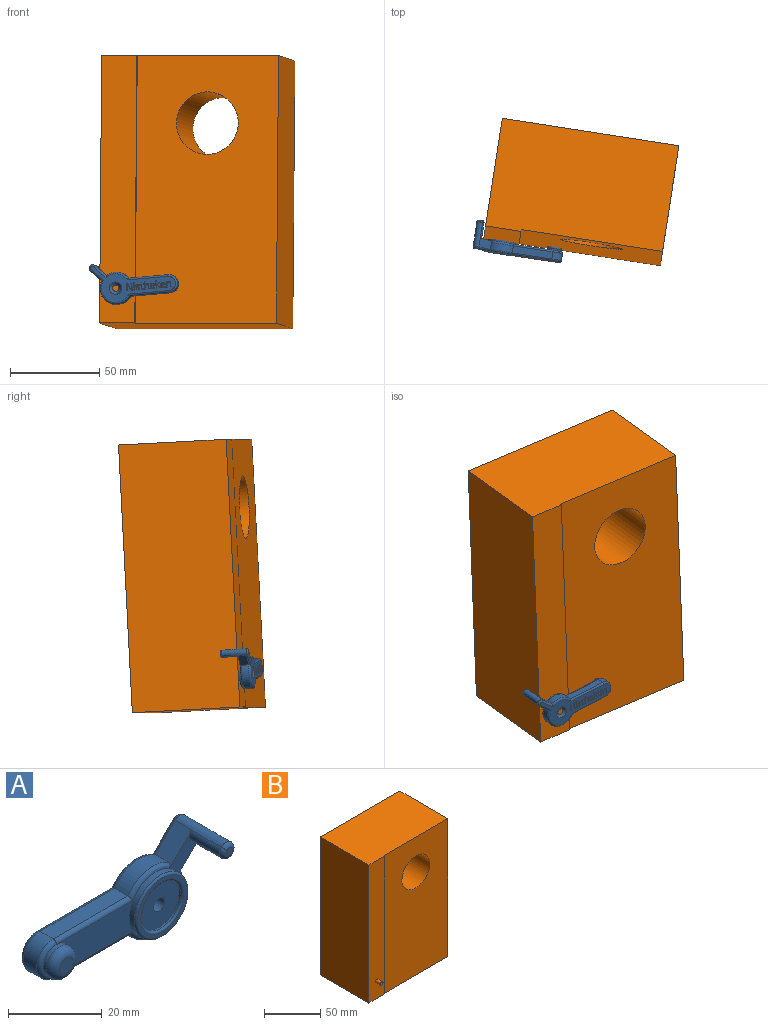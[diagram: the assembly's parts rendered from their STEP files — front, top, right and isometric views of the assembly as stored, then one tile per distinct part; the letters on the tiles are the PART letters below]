
ASSEMBLY  parts=2 mates=1
PART A: 218 faces, bbox 49.6x16x23.9 mm
  f0: plane 47.2x21.2mm, normal (0,1,0), area 355.5mm2, adj f16,f23,f24,f25,f26,f27,f28,f29
  f1: plane 23.07x8mm, normal (0,-1,0), area 153.6mm2, adj f12,f13,f32,f35
  f2: plane 9.55x9.55mm, normal (0,-1,0), area 31.1mm2, adj f7,f9,f13,f21
  f3: cylinder r=1.7mm len=5.23mm, axis (0,1,0), area 55.9mm2, adj f16,f18
  f4: cylinder r=5mm len=10mm, axis (0,1,0), area 62.8mm2, adj f5,f11,f24,f33
  f5: plane 22.52x4mm, normal (0,0,-1), area 90.1mm2, adj f4,f6,f26,f32
  f6: cylinder r=9mm len=16.48mm, axis (0,1,0), area 112.1mm2, adj f5,f7,f28,f31
  f7: plane 6.72x6.72mm, normal (0.71,0,-0.71), area 42.6mm2, adj f2,f6,f8,f30,f31
  f8: extruded ~14x3.41mm, area 88mm2, adj f7,f9,f21,f29,f37
  f9: plane 6.72x6.72mm, normal (-0.71,0,0.71), area 42.6mm2, adj f2,f8,f10,f27,f34
  f10: cylinder r=9mm len=12.27mm, axis (0,1,0), area 55.6mm2, adj f9,f11,f25,f34
  f11: plane 22.52x4mm, normal (0,0,1), area 90.1mm2, adj f4,f10,f23,f35
  f12: cylinder r=4mm len=8mm, axis (0,1,0), area 25.1mm2, adj f1,f33,f38
  f13: cylinder r=8mm len=16mm, axis (0,1,0), area 75.4mm2, adj f1,f2,f20,f31,f34
  f14: plane 15x15mm, normal (0,-1,0), area 44mm2, adj f19,f20
  f15: plane 4x4mm, normal (0,-1,0), area 12.6mm2, adj f38
  f16: cone r=1.7mm half-angle=45deg, axis (0,1,0), area 40.7mm2, adj f0,f3
  f17: cylinder r=6mm len=12mm, axis (0,-1,0), area 18.8mm2, adj f18,f19
  f18: plane 12x12mm, normal (0,-1,0), area 104mm2, adj f3,f17
  f19: torus R=6.5mm, axis (0,-1,0), area 30.5mm2, adj f14,f17
  f20: torus R=7.5mm, axis (0,-1,0), area 38.6mm2, adj f13,f14
  f21: cylinder r=2mm len=9mm, axis (0,1,0), area 56.5mm2, adj f2,f8,f36
  f22: plane 2x2mm, normal (0,-1,0), area 3.1mm2, adj f36,f37
  f23: cylinder r=1mm len=23.07mm, axis (-1,0,0), area 35.7mm2, adj f0,f11,f24,f25
  f24: torus R=4mm, axis (0,-1,0), area 22.9mm2, adj f0,f4,f23,f26
  f25: torus R=8mm, axis (0,-1,0), area 21.7mm2, adj f0,f10,f23,f27
  f26: cylinder r=1mm len=23.07mm, axis (1,0,0), area 35.7mm2, adj f0,f5,f24,f28
  f27: cylinder r=1mm len=7.29mm, axis (-0.71,0,-0.71), area 13.8mm2, adj f0,f9,f25,f29
  f28: torus R=8mm, axis (0,-1,0), area 43mm2, adj f0,f6,f26,f30
  f29: bspline ~4.36x4.36mm, area 8.1mm2, adj f0,f8,f27,f30
  f30: cylinder r=1mm len=7.29mm, axis (0.71,0,0.71), area 13.8mm2, adj f0,f7,f28,f29
  f31: torus R=8mm, axis (0,-1,0), area 42.4mm2, adj f6,f7,f13,f32
  f32: cylinder r=1mm len=23.07mm, axis (-1,0,0), area 35.7mm2, adj f1,f5,f31,f33
  f33: torus R=4mm, axis (0,-1,0), area 22.9mm2, adj f4,f12,f32,f35
  f34: torus R=8mm, axis (0,-1,0), area 21.1mm2, adj f9,f10,f13,f35
  f35: cylinder r=1mm len=23.07mm, axis (1,0,0), area 35.7mm2, adj f1,f11,f33,f34
  f36: torus R=1mm, axis (0,-1,0), area 8.1mm2, adj f21,f22,f37
  f37: bspline ~4.36x3.77mm, area 8.1mm2, adj f8,f22,f36
  f38: torus R=2mm, axis (0,-1,0), area 64.6mm2, adj f12,f15
  f39: plane 2.97x1mm, normal (1,0,0), area 3mm2, adj f0,f40,f42,f43
  f40: plane 1x0.45mm, normal (0,0,1), area 0.5mm2, adj f0,f39,f41,f43
  f41: plane 2.97x1mm, normal (-1,0,0), area 3mm2, adj f0,f40,f42,f43
  f42: plane 1x0.45mm, normal (0,0,-1), area 0.5mm2, adj f0,f39,f41,f43
  f43: plane 2.97x0.45mm, normal (0,1,0), area 1.3mm2, adj f39,f40,f41,f42
  f44: extruded ~1x0.23mm, area 0.2mm2, adj f0,f45,f51,f52
  f45: extruded ~1x0.23mm, area 0.2mm2, adj f0,f44,f46,f52
  f46: extruded ~1x0.19mm, area 0.2mm2, adj f0,f45,f47,f52
  f47: extruded ~1x0.19mm, area 0.2mm2, adj f0,f46,f48,f52
  f48: extruded ~1x0.23mm, area 0.2mm2, adj f0,f47,f49,f52
  f49: extruded ~1x0.23mm, area 0.2mm2, adj f0,f48,f50,f52
  f50: extruded ~1x0.19mm, area 0.2mm2, adj f0,f49,f51,f52
  f51: extruded ~1x0.19mm, area 0.2mm2, adj f0,f44,f50,f52
  f52: plane 0.6x0.53mm, normal (0,1,0), area 0.3mm2, adj f44,f45,f46,f47,f48,f49,f50,f51
  f53: extruded ~1x0.49mm, area 0.5mm2, adj f0,f54,f77,f78
  f54: extruded ~1x0.64mm, area 0.7mm2, adj f0,f53,f55,f78
  f55: extruded ~1x0.87mm, area 0.9mm2, adj f0,f54,f56,f78
  f56: extruded ~1x0.92mm, area 1mm2, adj f0,f55,f57,f78
  f57: plane 1x0.42mm, normal (-1,0,0), area 0.4mm2, adj f0,f56,f58,f78
  f58: extruded ~1x0.46mm, area 0.5mm2, adj f0,f57,f59,f78
  f59: extruded ~1x0.47mm, area 0.5mm2, adj f0,f58,f60,f78
  f60: extruded ~1x0.54mm, area 0.6mm2, adj f0,f59,f61,f78
  f61: extruded ~1x0.34mm, area 0.4mm2, adj f0,f60,f62,f78
  f62: extruded ~1x0.3mm, area 0.3mm2, adj f0,f61,f63,f78
  f63: extruded ~1x0.59mm, area 0.7mm2, adj f0,f62,f64,f78
  f64: extruded ~1x0.59mm, area 0.6mm2, adj f0,f63,f65,f78
  f65: extruded ~1x0.26mm, area 0.4mm2, adj f0,f64,f66,f78
  f66: extruded ~1x0.35mm, area 0.4mm2, adj f0,f65,f67,f78
  f67: extruded ~1x0.57mm, area 0.7mm2, adj f0,f66,f68,f78
  f68: extruded ~1x0.81mm, area 0.9mm2, adj f0,f67,f69,f78
  f69: extruded ~1x0.94mm, area 1mm2, adj f0,f68,f70,f78
  f70: plane 1x0.37mm, normal (0.92,0,0.4), area 0.4mm2, adj f0,f69,f71,f78
  f71: extruded ~1x0.81mm, area 0.8mm2, adj f0,f70,f72,f78
  f72: extruded ~1x0.48mm, area 0.5mm2, adj f0,f71,f73,f78
  f73: extruded ~1x0.28mm, area 0.3mm2, adj f0,f72,f74,f78
  f74: extruded ~1x0.2mm, area 0.2mm2, adj f0,f73,f75,f78
  f75: extruded ~1x0.2mm, area 0.3mm2, adj f0,f74,f76,f78
  f76: extruded ~1x0.52mm, area 0.6mm2, adj f0,f75,f77,f78
  f77: extruded ~1x0.71mm, area 0.8mm2, adj f0,f53,f76,f78
  f78: plane 3.08x2.11mm, normal (0,1,0), area 2.7mm2, adj f53,f54,f55,f56,f57,f58,f59,f60
  f79: extruded ~1x0.35mm, area 0.4mm2, adj f0,f80,f97,f98
  f80: extruded ~1x0.23mm, area 0.2mm2, adj f0,f79,f81,f98
  f81: extruded ~1x0.18mm, area 0.2mm2, adj f0,f80,f82,f98
  f82: plane 1x0.34mm, normal (1,0,0), area 0.3mm2, adj f0,f81,f83,f98
  f83: extruded ~1x0.22mm, area 0.2mm2, adj f0,f82,f84,f98
  f84: extruded ~1x0.26mm, area 0.3mm2, adj f0,f83,f85,f98
  f85: extruded ~1x0.91mm, area 1.4mm2, adj f0,f84,f86,f98
  f86: plane 1.77x1mm, normal (-1,0,0), area 1.8mm2, adj f0,f85,f87,f98
  f87: plane 1x0.43mm, normal (0,0,1), area 0.4mm2, adj f0,f86,f88,f98
  f88: plane 1x0.22mm, normal (-1,0,0), area 0.2mm2, adj f0,f87,f89,f98
  f89: plane 1x0.43mm, normal (-0.4,0,-0.92), area 0.5mm2, adj f0,f88,f90,f98
  f90: plane 1x0.63mm, normal (-0.96,0,-0.29), area 0.7mm2, adj f0,f89,f91,f98
  f91: plane 1x0.26mm, normal (0,0,-1), area 0.3mm2, adj f0,f90,f92,f98
  f92: plane 1x0.69mm, normal (1,0,0), area 0.7mm2, adj f0,f91,f93,f98
  f93: plane 1x0.86mm, normal (0,0,-1), area 0.9mm2, adj f0,f92,f94,f98
  f94: plane 1x0.35mm, normal (1,0,0), area 0.3mm2, adj f0,f93,f95,f98
  f95: plane 1x0.86mm, normal (0,0,1), area 0.9mm2, adj f0,f94,f96,f98
  f96: plane 1.75x1mm, normal (1,0,0), area 1.8mm2, adj f0,f95,f97,f98
  f97: extruded ~1x0.41mm, area 0.4mm2, adj f0,f79,f96,f98
  f98: plane 3.72x1.76mm, normal (0,1,0), area 2.3mm2, adj f79,f80,f81,f82,f83,f84,f85,f86
  f99: plane 1x0.33mm, normal (0,0,1), area 0.3mm2, adj f0,f100,f125,f126
  f100: plane 1x0.42mm, normal (-0.98,0,0.21), area 0.4mm2, adj f0,f99,f101,f126
  f101: plane 1x0.02mm, normal (0,0,1), area 0mm2, adj f0,f100,f102,f126
  f102: extruded ~1x0.44mm, area 0.6mm2, adj f0,f101,f103,f126
  f103: extruded ~1x0.55mm, area 0.6mm2, adj f0,f102,f104,f126
  f104: extruded ~1x0.69mm, area 0.7mm2, adj f0,f103,f105,f126
  f105: extruded ~1x0.65mm, area 0.7mm2, adj f0,f104,f106,f126
  f106: extruded ~1.44x1mm, area 1.9mm2, adj f0,f105,f107,f126
  f107: plane 1x0.5mm, normal (-0.03,0,-1), area 0.5mm2, adj f0,f106,f108,f126
  f108: plane 1x0.19mm, normal (-1,0,0), area 0.2mm2, adj f0,f107,f109,f126
  f109: extruded ~1x0.52mm, area 0.5mm2, adj f0,f108,f110,f126
  f110: extruded ~1x0.48mm, area 0.5mm2, adj f0,f109,f111,f126
  f111: extruded ~1x0.84mm, area 0.9mm2, adj f0,f110,f112,f126
  f112: plane 1x0.34mm, normal (-0.93,0,0.37), area 0.4mm2, adj f0,f111,f113,f126
  f113: extruded ~1x0.48mm, area 0.5mm2, adj f0,f112,f114,f126
  f114: extruded ~1x0.53mm, area 0.5mm2, adj f0,f113,f115,f126
  f115: extruded ~1x0.79mm, area 0.8mm2, adj f0,f114,f116,f126
  f116: extruded ~1x0.76mm, area 0.8mm2, adj f0,f115,f125,f126
  f117: extruded ~1x0.41mm, area 0.4mm2, adj f118,f124,f126,f127
  f118: extruded ~1x0.66mm, area 0.7mm2, adj f117,f119,f126,f127
  f119: extruded ~1x0.65mm, area 0.7mm2, adj f118,f120,f126,f127
  f120: plane 1x0.27mm, normal (-1,0,0), area 0.3mm2, adj f119,f121,f126,f127
  f121: plane 1x0.45mm, normal (0.04,0,1), area 0.5mm2, adj f120,f122,f126,f127
  f122: extruded ~1x0.77mm, area 0.8mm2, adj f121,f123,f126,f127
  f123: extruded ~1x0.46mm, area 0.5mm2, adj f122,f124,f126,f127
  f124: extruded ~1x0.37mm, area 0.4mm2, adj f117,f123,f126,f127
  f125: plane 2.03x1mm, normal (1,0,0), area 2mm2, adj f0,f99,f116,f126
  f126: plane 3.08x2.38mm, normal (0,1,0), area 3.5mm2, adj f99,f100,f101,f102,f103,f104,f105,f106
  f127: plane 1.46x1.14mm, normal (0,1,0), area 1.3mm2, adj f117,f118,f119,f120,f121,f122,f123,f124
  f128: plane 1x0.45mm, normal (0,0,1), area 0.5mm2, adj f0,f129,f144,f145
  f129: plane 1.92x1mm, normal (-1,0,0), area 1.9mm2, adj f0,f128,f130,f145
  f130: extruded ~1x0.54mm, area 0.6mm2, adj f0,f129,f131,f145
  f131: extruded ~1x0.52mm, area 0.6mm2, adj f0,f130,f132,f145
  f132: extruded ~1x0.68mm, area 0.8mm2, adj f0,f131,f133,f145
  f133: extruded ~1x0.83mm, area 0.9mm2, adj f0,f132,f134,f145
  f134: plane 1.56x1mm, normal (1,0,0), area 1.6mm2, adj f0,f133,f135,f145
  f135: plane 1x0.45mm, normal (0,0,1), area 0.5mm2, adj f0,f134,f136,f145
  f136: plane 2.97x1mm, normal (-1,0,0), area 3mm2, adj f0,f135,f137,f145
  f137: plane 1x0.37mm, normal (0,0,-1), area 0.4mm2, adj f0,f136,f138,f145
  f138: plane 1x0.41mm, normal (0.98,0,-0.18), area 0.4mm2, adj f0,f137,f139,f145
  f139: plane 1x0.02mm, normal (0,0,-1), area 0mm2, adj f0,f138,f140,f145
  f140: extruded ~1x0.39mm, area 0.5mm2, adj f0,f139,f141,f145
  f141: extruded ~1x0.56mm, area 0.6mm2, adj f0,f140,f142,f145
  f142: extruded ~1x0.81mm, area 0.9mm2, adj f0,f141,f143,f145
  f143: extruded ~1x0.83mm, area 0.9mm2, adj f0,f142,f144,f145
  f144: plane 1.94x1mm, normal (1,0,0), area 1.9mm2, adj f0,f128,f143,f145
  f145: plane 3.03x2.49mm, normal (0,1,0), area 3.2mm2, adj f128,f129,f130,f131,f132,f133,f134,f135
  f146: plane 1x0.02mm, normal (0,0,-1), area 0mm2, adj f0,f147,f160,f161
  f147: extruded ~1x0.43mm, area 0.6mm2, adj f0,f146,f148,f161
  f148: plane 1.02x1mm, normal (-0.73,0,-0.69), area 1.4mm2, adj f0,f147,f149,f161
  f149: plane 1x0.53mm, normal (0,0,-1), area 0.5mm2, adj f0,f148,f150,f161
  f150: plane 1.27x1.21mm, normal (0.72,0,0.69), area 1.7mm2, adj f0,f149,f151,f161
  f151: plane 1.71x1.29mm, normal (0.8,0,-0.6), area 2.1mm2, adj f0,f150,f152,f161
  f152: plane 1x0.55mm, normal (0,0,1), area 0.5mm2, adj f0,f151,f153,f161
  f153: plane 1.41x1.05mm, normal (-0.8,0,0.6), area 1.8mm2, adj f0,f152,f154,f161
  f154: plane 1x0.34mm, normal (0.65,0,0.76), area 0.4mm2, adj f0,f153,f155,f161
  f155: plane 1.11x1mm, normal (1,0,0), area 1.1mm2, adj f0,f154,f156,f161
  f156: plane 1x0.45mm, normal (0,0,1), area 0.4mm2, adj f0,f155,f157,f161
  f157: plane 4.22x1mm, normal (-1,0,0), area 4.2mm2, adj f0,f156,f158,f161
  f158: plane 1x0.45mm, normal (0,0,-1), area 0.4mm2, adj f0,f157,f159,f161
  f159: plane 2.24x1mm, normal (1,0,0), area 2.2mm2, adj f0,f158,f160,f161
  f160: extruded ~1x0.46mm, area 0.5mm2, adj f0,f146,f159,f161
  f161: plane 4.22x2.38mm, normal (0,1,0), area 3.6mm2, adj f146,f147,f148,f149,f150,f151,f152,f153
  f162: plane 1x0.45mm, normal (0,0,1), area 0.5mm2, adj f0,f163,f179,f180
  f163: plane 1.92x1mm, normal (-1,0,0), area 1.9mm2, adj f0,f162,f164,f180
  f164: extruded ~1x0.54mm, area 0.6mm2, adj f0,f163,f165,f180
  f165: extruded ~1x0.52mm, area 0.6mm2, adj f0,f164,f166,f180
  f166: extruded ~1x0.68mm, area 0.8mm2, adj f0,f165,f167,f180
  f167: extruded ~1x0.84mm, area 0.9mm2, adj f0,f166,f168,f180
  f168: plane 1.55x1mm, normal (1,0,0), area 1.6mm2, adj f0,f167,f169,f180
  f169: plane 1x0.45mm, normal (0,0,1), area 0.5mm2, adj f0,f168,f170,f180
  f170: plane 4.22x1mm, normal (-1,0,0), area 4.2mm2, adj f0,f169,f171,f180
  f171: plane 1x0.45mm, normal (0,0,-1), area 0.5mm2, adj f0,f170,f172,f180
  f172: plane 1.28x1mm, normal (1,0,0), area 1.3mm2, adj f0,f171,f173,f180
  f173: extruded ~1x0.38mm, area 0.4mm2, adj f0,f172,f174,f180
  f174: plane 1x0.03mm, normal (0,0,-1), area 0mm2, adj f0,f173,f175,f180
  f175: extruded ~1x0.38mm, area 0.5mm2, adj f0,f174,f176,f180
  f176: extruded ~1x0.56mm, area 0.6mm2, adj f0,f175,f177,f180
  f177: extruded ~1x0.82mm, area 0.9mm2, adj f0,f176,f178,f180
  f178: extruded ~1x0.82mm, area 0.9mm2, adj f0,f177,f179,f180
  f179: plane 1.94x1mm, normal (1,0,0), area 1.9mm2, adj f0,f162,f178,f180
  f180: plane 4.22x2.49mm, normal (0,1,0), area 3.8mm2, adj f162,f163,f164,f165,f166,f167,f168,f169
  f181: extruded ~1x0.51mm, area 0.5mm2, adj f0,f182,f199,f200
  f182: extruded ~1.04x1mm, area 1.1mm2, adj f0,f181,f183,f200
  f183: extruded ~1.11x1mm, area 1.2mm2, adj f0,f182,f184,f200
  f184: extruded ~1.14x1mm, area 1.2mm2, adj f0,f183,f185,f200
  f185: extruded ~1x0.95mm, area 1.1mm2, adj f0,f184,f186,f200
  f186: extruded ~1x0.88mm, area 1mm2, adj f0,f185,f187,f200
  f187: extruded ~1x0.97mm, area 1mm2, adj f0,f186,f188,f200
  f188: plane 1x0.28mm, normal (1,0,0), area 0.3mm2, adj f0,f187,f189,f200
  f189: plane 2.05x1mm, normal (0,0,1), area 2mm2, adj f0,f188,f190,f200
  f190: extruded ~1x0.79mm, area 0.9mm2, adj f0,f189,f191,f200
  f191: extruded ~1x0.71mm, area 0.8mm2, adj f0,f190,f192,f200
  f192: extruded ~1x0.95mm, area 1mm2, adj f0,f191,f193,f200
  f193: plane 1x0.4mm, normal (1,0,0), area 0.4mm2, adj f0,f192,f199,f200
  f194: extruded ~1x0.54mm, area 0.6mm2, adj f195,f198,f200,f201
  f195: extruded ~1x0.57mm, area 0.6mm2, adj f194,f196,f200,f201
  f196: extruded ~1x0.65mm, area 0.7mm2, adj f195,f197,f200,f201
  f197: plane 1.55x1mm, normal (0,0,-1), area 1.6mm2, adj f196,f198,f200,f201
  f198: extruded ~1x0.65mm, area 0.7mm2, adj f194,f197,f200,f201
  f199: extruded ~1x0.45mm, area 0.5mm2, adj f0,f181,f193,f200
  f200: plane 3.08x2.51mm, normal (0,1,0), area 3.5mm2, adj f181,f182,f183,f184,f185,f186,f187,f188
  f201: plane 1.55x0.88mm, normal (0,1,0), area 1.1mm2, adj f194,f195,f196,f197,f198
  f202: plane 3.97x1mm, normal (1,0,0), area 4mm2, adj f0,f203,f216,f217
  f203: plane 1x0.53mm, normal (0,0,1), area 0.5mm2, adj f0,f202,f204,f217
  f204: plane 3.33x2.17mm, normal (-0.84,0,0.55), area 4mm2, adj f0,f203,f205,f217
  f205: plane 1x0.02mm, normal (0,0,1), area 0mm2, adj f0,f204,f206,f217
  f206: extruded ~1.07x1mm, area 1.1mm2, adj f0,f205,f207,f217
  f207: plane 2.25x1mm, normal (1,0,0), area 2.3mm2, adj f0,f206,f208,f217
  f208: plane 1x0.43mm, normal (0,0,1), area 0.4mm2, adj f0,f207,f209,f217
  f209: plane 3.97x1mm, normal (-1,0,0), area 4mm2, adj f0,f208,f210,f217
  f210: plane 1x0.52mm, normal (0,0,-1), area 0.5mm2, adj f0,f209,f211,f217
  f211: plane 3.32x2.16mm, normal (0.84,0,-0.55), area 4mm2, adj f0,f210,f212,f217
  f212: plane 1x0.02mm, normal (0,0,-1), area 0mm2, adj f0,f211,f213,f217
  f213: extruded ~1x0.47mm, area 0.5mm2, adj f0,f212,f214,f217
  f214: extruded ~1x0.57mm, area 0.6mm2, adj f0,f213,f215,f217
  f215: plane 2.28x1mm, normal (-1,0,0), area 2.3mm2, adj f0,f214,f216,f217
  f216: plane 1x0.43mm, normal (0,0,-1), area 0.4mm2, adj f0,f202,f215,f217
  f217: plane 3.97x3.1mm, normal (0,1,0), area 5.2mm2, adj f202,f203,f204,f205,f206,f207,f208,f209
PART B: 11 faces, bbox 100x67x150 mm
  f0: plane 150x61mm, normal (-1,0,0), area 9150mm2, adj f1,f3,f6,f8
  f1: plane 100x61mm, normal (0,0,-1), area 6020mm2, adj f0,f2,f5,f6,f7,f8
  f2: plane 150x60mm, normal (1,0,0), area 9000mm2, adj f1,f3,f5,f6
  f3: plane 100x61mm, normal (0,0,1), area 6020mm2, adj f0,f2,f5,f6,f7,f8
  f4: cylinder r=17.5mm len=60mm, axis (0,1,0), area 6597.3mm2, adj f5,f6
  f5: plane 150x80mm, normal (0,-1,0), area 11037.9mm2, adj f1,f2,f3,f4,f7
  f6: plane 150x100mm, normal (0,1,0), area 14037.9mm2, adj f0,f1,f2,f3,f4
  f7: plane 150x1mm, normal (1,0,0), area 150mm2, adj f1,f3,f5,f8
  f8: plane 150x20mm, normal (0,-1,0), area 2990.4mm2, adj f0,f1,f3,f7,f9
  f9: cylinder r=1.75mm len=6mm, axis (0,1,0), area 66mm2, adj f8,f10
  f10: plane 3.5x3.5mm, normal (0,-1,0), area 9.6mm2, adj f9
PLACE A rot(axis=(-0.04,0.03,1),171.3deg) t=(-155.23,-61.5,57.47)mm
PLACE B rot(axis=(-0.32,0.02,-0.95),9.3deg) t=(-184.03,10.27,27.22)mm fixed
MATE revolute A.f3 <-> B.f9  axis (0.15,0.99,-0.05) through (-183.33,-50.47,49.54)mm
